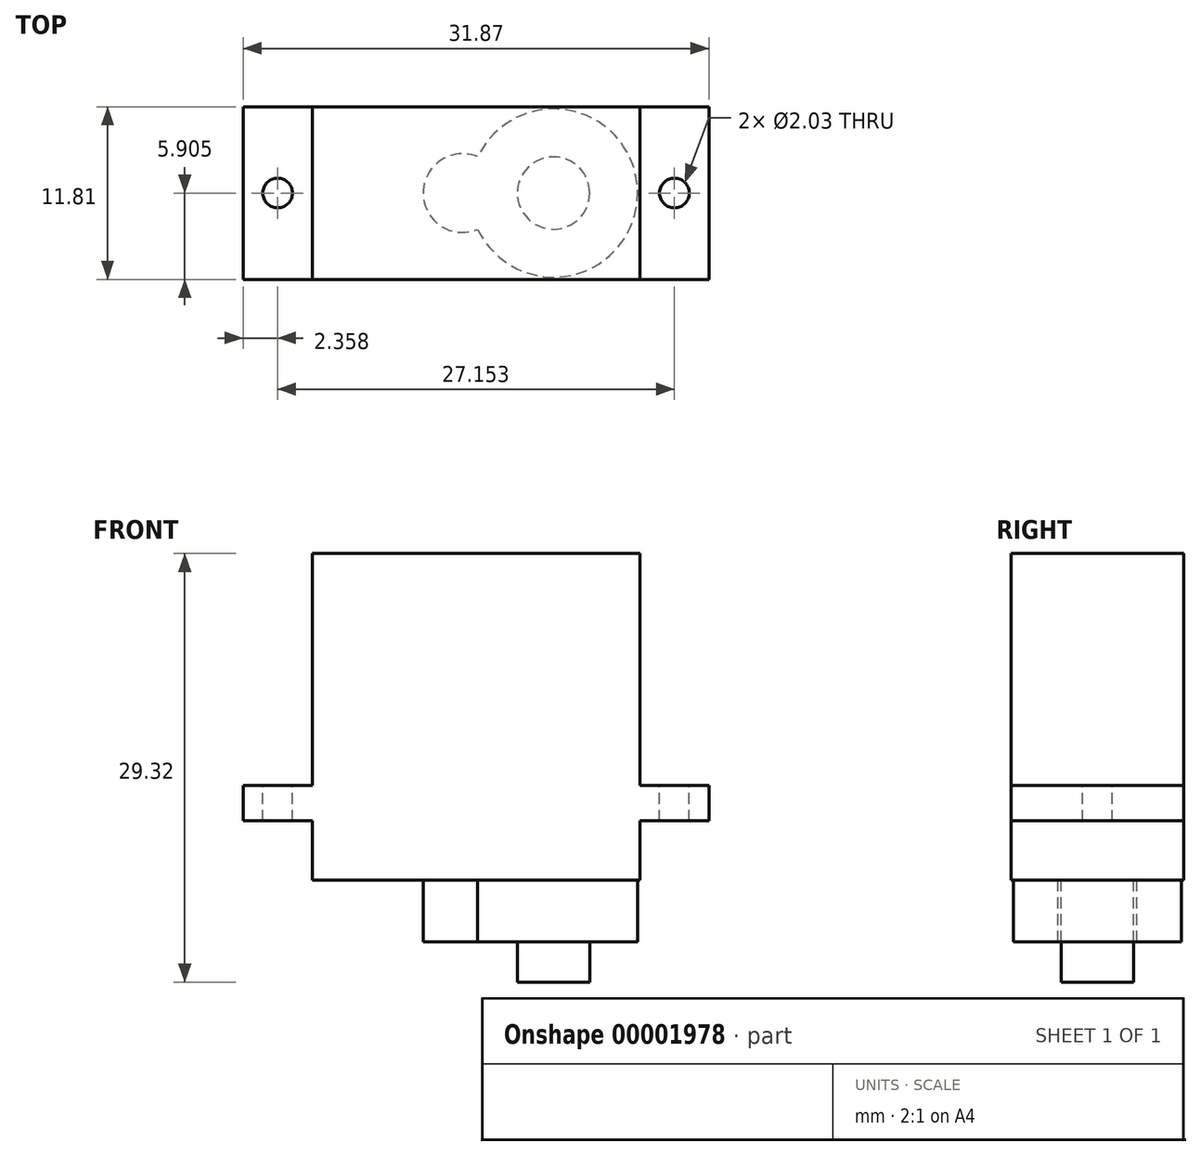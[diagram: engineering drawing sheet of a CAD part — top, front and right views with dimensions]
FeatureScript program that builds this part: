
annotation { "Feature Type Name" : "Feature", "Feature Type Description" : "" }
export const myFeature = defineFeature(function(context is Context, id is Id, definition is map)
    precondition{}
    {
        {
            var Q0;
            Q0=qCreatedBy(makeId("Top.planeOp"),FACE);
            var sketch = newSketch(context, id + "F0", { "sketchPlane" : qUnion([Q0])});
            skLineSegment(sketch, "E0.bottom", {"start": v(0, 0) * mm, "end": v(22.43, 0) * mm});
            skLineSegment(sketch, "E0.top", {"start": v(0, 11.81) * mm, "end": v(22.43, 11.81) * mm});
            skLineSegment(sketch, "E0.left", {"start": v(0, 0) * mm, "end": v(0, 11.81) * mm});
            skLineSegment(sketch, "E0.right", {"start": v(22.43, 0) * mm, "end": v(22.43, 11.81) * mm});
            skLineSegment(sketch, "E1", {"start": v(0, 11.81) * mm, "end": v(-4.72, 11.81) * mm});
            skLineSegment(sketch, "E2", {"start": v(-4.72, 11.81) * mm, "end": v(-4.72, 0) * mm});
            skLineSegment(sketch, "E3", {"start": v(-4.72, 0) * mm, "end": v(0, 0) * mm});
            skLineSegment(sketch, "E4", {"start": v(22.43, 11.81) * mm, "end": v(27.15, 11.81) * mm});
            skLineSegment(sketch, "E5", {"start": v(27.15, 11.81) * mm, "end": v(27.15, 0) * mm});
            skLineSegment(sketch, "E6", {"start": v(27.15, 0) * mm, "end": v(22.43, 0) * mm});
            skCircle(sketch, "E7", {"center": v(-2.36, 5.9) * mm, "radius": 1.02 * mm});
            skLineSegment(sketch, "E8", {"start": v(-2.36, 5.9) * mm, "end": v(0, 5.9) * mm, "construction": true});
            skLineSegment(sketch, "E9", {"start": v(11.21, 11.81) * mm, "end": v(11.21, 0) * mm, "construction": true});
            skCircle(sketch, "E10.0.MirrorC", {"center": v(24.8, 5.9) * mm, "radius": 1.02 * mm});
            skSolve(sketch);
        }
        {
            var Q0;
            Q0=makeQuery(id+"F0.imprint","IMPRINT",FACE,{"disambiguationData":[TD([[makeQuery(id+"F0.imprint","IMPRINT",EDGE,{"derivedFrom":sQuery(id+"F0.wireOp",EDGE,"E0.bottom")}),1.0]])]});
            extrude(context, id + "F1", {"entities" : qUnion([Q0]), "depth" : 15.88 * mm});
        }
        {
            var Q0;
            Q0=makeQuery(id+"F0.imprint","IMPRINT",FACE,{"disambiguationData":[TD([[makeQuery(id+"F0.imprint","IMPRINT",EDGE,{"derivedFrom":sQuery(id+"F0.wireOp",EDGE,"E0.bottom")}),1.0]])]});
            extrude(context, id + "F2", {"entities" : qUnion([Q0]), "operationType" : NewBodyOperationType.ADD, "oppositeDirection" : true, "depth" : 6.48 * mm});
        }
        {
            var Q0;
            Q0=makeQuery(id+"F0.imprint","IMPRINT",FACE,{"disambiguationData":[TD([[makeQuery(id+"F0.imprint","IMPRINT",EDGE,{"derivedFrom":sQuery(id+"F0.wireOp",EDGE,"E0.left")}),1.0]])]});
            var Q1;
            Q1=makeQuery(id+"F0.imprint","IMPRINT",FACE,{"disambiguationData":[TD([[makeQuery(id+"F0.imprint","IMPRINT",EDGE,{"derivedFrom":sQuery(id+"F0.wireOp",EDGE,"E0.right")}),-1.0]])]});
            extrude(context, id + "F3", {"entities" : qUnion([Q0, Q1]), "operationType" : NewBodyOperationType.ADD, "oppositeDirection" : true, "depth" : 2.41 * mm});
        }
        {
            var Q0;
            Q0=makeQuery(id+"F2.opExtrude","CAP_FACE",FACE,{"disambiguationData":[OSD([sQuery(id+"F0.wireOp",EDGE,"E0.bottom"),sQuery(id+"F0.wireOp",EDGE,"E0.top"),sQuery(id+"F0.wireOp",EDGE,"E0.left"),sQuery(id+"F0.wireOp",EDGE,"E0.right")])],"isStart":false});
            var sketch = newSketch(context, id + "F4", { "sketchPlane" : qUnion([Q0])});
            skLineSegment(sketch, "E11", {"start": v(22.43, -5.9) * mm, "end": v(0, -5.9) * mm, "construction": true});
            skArc(sketch, "E12", {"start": v(11.33, -8.39) * mm, "mid": v(22.28, -5.9) * mm, "end": v(11.33, -3.42) * mm});
            skArc(sketch, "E13", {"start": v(11.33, -3.42) * mm, "mid": v(7.6, -5.9) * mm, "end": v(11.33, -8.39) * mm});
            skCircle(sketch, "E14", {"center": v(16.52, -5.9) * mm, "radius": 2.48 * mm});
            skSolve(sketch);
        }
        {
            var Q0;
            Q0=makeQuery(id+"F4.imprint","IMPRINT",FACE,{"disambiguationData":[TD([[makeQuery(id+"F4.imprint","IMPRINT",EDGE,{"derivedFrom":sQuery(id+"F4.wireOp",EDGE,"E12")}),1.0]])]});
            extrude(context, id + "F5", {"entities" : qUnion([Q0]), "operationType" : NewBodyOperationType.ADD, "depth" : 4.22 * mm});
        }
        {
            var Q0;
            Q0=makeQuery(id+"F5.boolean.opBoolean","SPLIT",FACE,{"disambiguationData":[TD([makeQuery(id+"F5.opExtrude","SWEPT_FACE",FACE,{"disambiguationData":[OSD([sQuery(id+"F4.wireOp",EDGE,"E14")])]})])],"derivedFrom":makeQuery(id+"F2.opExtrude","CAP_FACE",FACE,{"disambiguationData":[OSD([sQuery(id+"F0.wireOp",EDGE,"E0.bottom"),sQuery(id+"F0.wireOp",EDGE,"E0.top"),sQuery(id+"F0.wireOp",EDGE,"E0.left"),sQuery(id+"F0.wireOp",EDGE,"E0.right")])],"isStart":false})});
            extrude(context, id + "F6", {"entities" : qUnion([Q0]), "operationType" : NewBodyOperationType.ADD, "depth" : 6.96 * mm});
        }
    });
